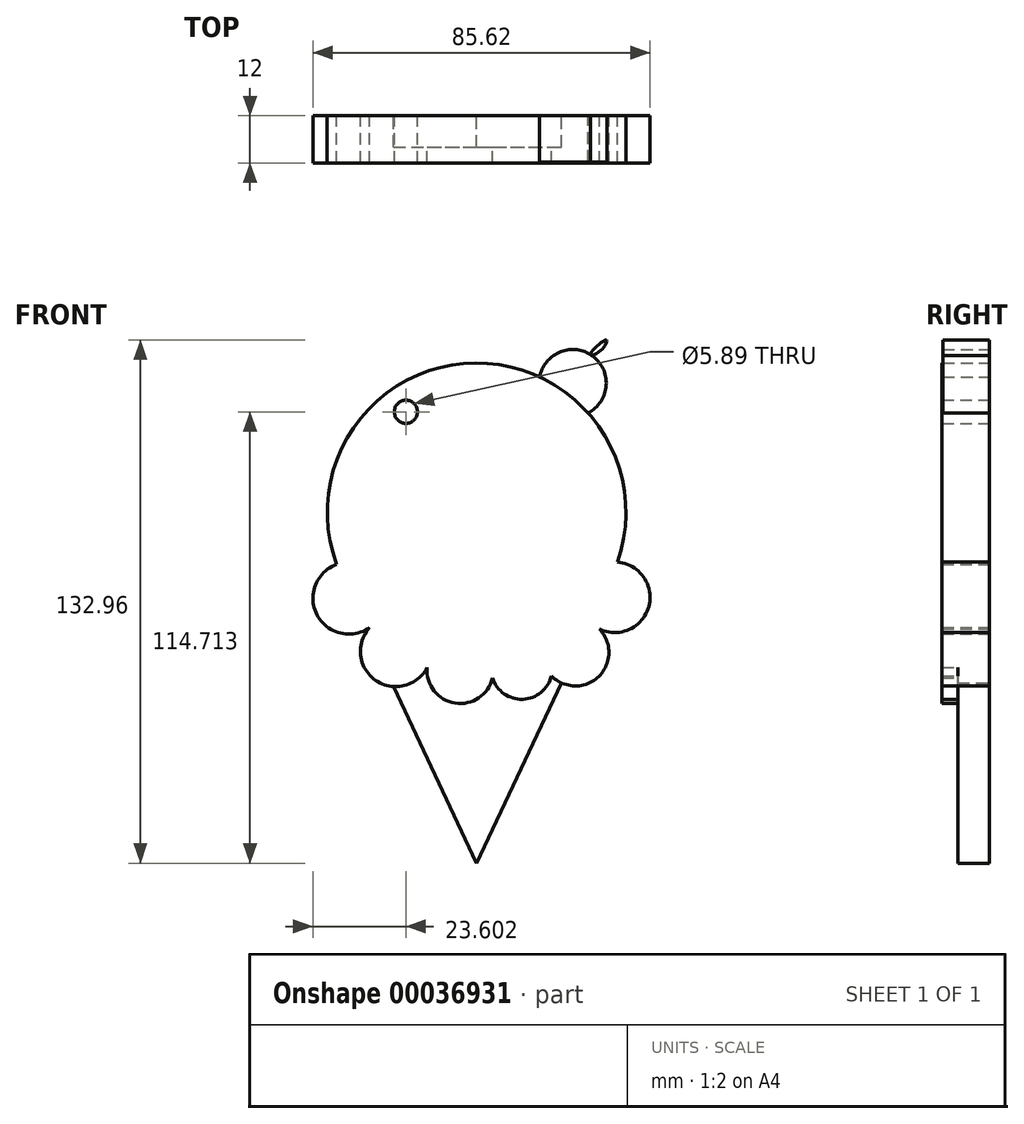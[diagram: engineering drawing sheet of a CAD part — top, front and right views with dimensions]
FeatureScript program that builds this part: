
annotation { "Feature Type Name" : "Feature", "Feature Type Description" : "" }
export const myFeature = defineFeature(function(context is Context, id is Id, definition is map)
    precondition{}
    {
        {
            var Q0;
            Q0=qCreatedBy(makeId("Front.planeOp"),FACE);
            var sketch = newSketch(context, id + "F0", { "sketchPlane" : qUnion([Q0])});
            skArc(sketch, "E0", {"start": v(35.76, 15.28) * mm, "mid": v(-0.3, 65.87) * mm, "end": v(-35.56, 14.72) * mm});
            skLineSegment(sketch, "E1", {"start": v(-27.9, -1.8) * mm, "end": v(-27.78, -2.06) * mm});
            skLineSegment(sketch, "E2", {"start": v(0, -61.23) * mm, "end": v(21.55, -15.39) * mm});
            skArc(sketch, "E3", {"start": v(-35.56, 14.72) * mm, "mid": v(-40.01, 1.05) * mm, "end": v(-25.67, 0) * mm});
            skArc(sketch, "E4", {"start": v(-27.2, -1.34) * mm, "mid": v(-24.14, -15.6) * mm, "end": v(-11.59, -8.19) * mm});
            skArc(sketch, "E5", {"start": v(-12.57, -11.53) * mm, "mid": v(-3.29, -20.58) * mm, "end": v(3.91, -9.8) * mm});
            skArc(sketch, "E6", {"start": v(4.03, -14.16) * mm, "mid": v(15.6, -18.35) * mm, "end": v(16.76, -6.1) * mm});
            skArc(sketch, "E7", {"start": v(19, -13.58) * mm, "mid": v(32.01, -12.64) * mm, "end": v(28.79, 0) * mm});
            skArc(sketch, "E8", {"start": v(31.16, -1.7) * mm, "mid": v(43.74, 4) * mm, "end": v(35.76, 15.28) * mm});
            skLineSegment(sketch, "E9.trimOffspring", {"start": v(-21.08, -16.33) * mm, "end": v(0, -61.23) * mm});
            skCircle(sketch, "E10", {"center": v(-17.97, 53.48) * mm, "radius": 2.94 * mm});
            skArc(sketch, "E11", {"start": v(28.3, 53.2) * mm, "mid": v(29.51, 67.62) * mm, "end": v(16.04, 62.31) * mm});
            skFitSpline(sketch, "E12", {"points": [v(28.89, 68.05) * mm, v(32.85, 71.73) * mm, v(31.72, 69.2) * mm, v(28.89, 68.05) * mm]});
            skSolve(sketch);
        }
        {
            var Q0;
            {var subQ7=sQuery(id+"F0.wireOp",EDGE,"E0");Q0=makeQuery(id+"F0.imprint","IMPRINT",FACE,{"disambiguationData":[TD([[makeQuery(id+"F0.imprint","IMPRINT",EDGE,{"derivedFrom":subQ7}),1.0]])]});}
            extrude(context, id + "F1", {"entities" : qUnion([Q0]), "depth" : 12 * mm});
        }
        {
            var Q0;
            {var subQ4=sQuery(id+"F0.wireOp",EDGE,"E2");Q0=makeQuery(id+"F0.imprint","IMPRINT",FACE,{"disambiguationData":[TD([[makeQuery(id+"F0.imprint","IMPRINT",EDGE,{"derivedFrom":subQ4}),1.0]])]});}
            extrude(context, id + "F2", {"entities" : qUnion([Q0]), "operationType" : NewBodyOperationType.ADD, "depth" : 8 * mm});
        }
        {
            var Q0;
            {var subQ1=sQuery(id+"F0.wireOp",EDGE,"E11");var subQ4=sQuery(id+"F0.wireOp",EDGE,"E0");var subQ6=makeQuery(id+"F0.imprint","INTERSECT",VERTEX,{"disambiguationData":[OD(0.0)],"derivedFrom":[subQ4,subQ1]});Q0=makeQuery(id+"F0.imprint","IMPRINT",FACE,{"disambiguationData":[TD([[makeQuery(id+"F0.imprint","IMPRINT",EDGE,{"disambiguationData":[TD([[subQ6,-1.0]])],"derivedFrom":subQ4}),-1.0]])]});}
            extrude(context, id + "F3", {"entities" : qUnion([Q0]), "operationType" : NewBodyOperationType.ADD, "depth" : 11.8 * mm});
        }
        {
            var Q0;
            {var subQ0=sQuery(id+"F0.wireOp",EDGE,"E12");var subQ1=sQuery(id+"F0.wireOp",EDGE,"E11");var subQ3=makeQuery(id+"F0.imprint","INTERSECT",VERTEX,{"disambiguationData":[OD(0.0)],"derivedFrom":[subQ1,subQ0]});Q0=makeQuery(id+"F0.imprint","IMPRINT",FACE,{"disambiguationData":[TD([[makeQuery(id+"F0.imprint","IMPRINT",EDGE,{"disambiguationData":[TD([[subQ3,-1.0]])],"derivedFrom":subQ1}),-1.0]])]});}
            extrude(context, id + "F4", {"entities" : qUnion([Q0]), "depth" : 11.8 * mm});
        }
    });
